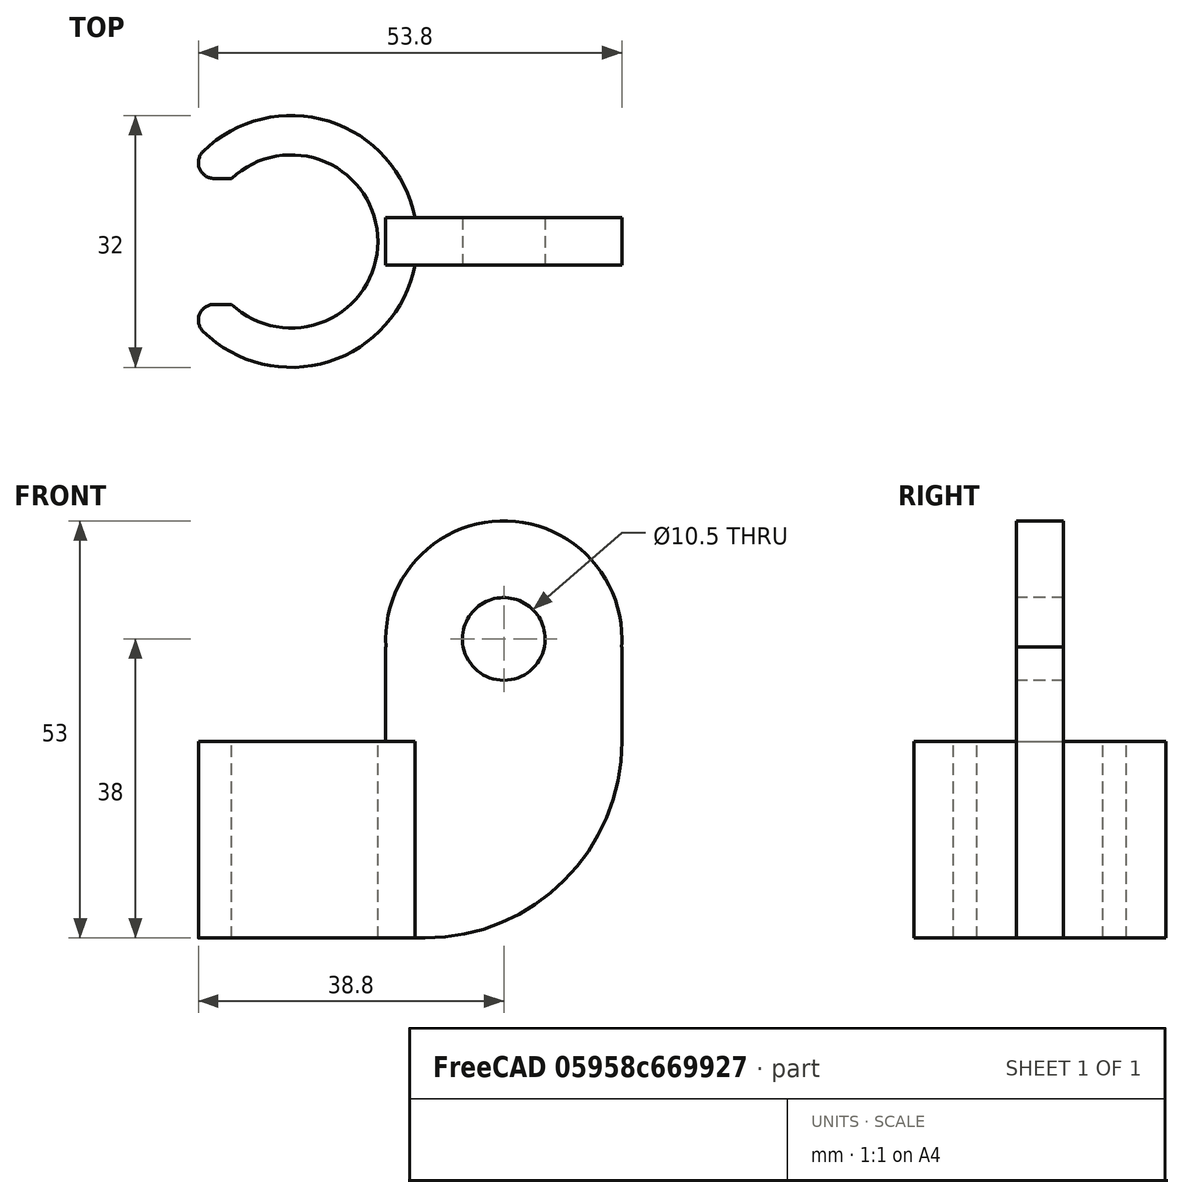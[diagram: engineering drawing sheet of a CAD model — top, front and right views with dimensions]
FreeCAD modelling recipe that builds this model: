
FCSTD DOCUMENT  (FreeCAD 0.18R4 (GitTag))
Label: Soporte_Ducha
License: All rights reserved
LicenseURL: http://en.wikipedia.org/wiki/All_rights_reserved
objects: Part::Cylinder×4, Part::Cut×3, Part::Box×2, Part::MultiFuse×2, Part::Fillet×2
note: 13 computed .brp shape members not serialized (recipe doc carries the construction recipe); baked Part::Feature solids carry a one-line shape summary decoded from their .brp

FEATURE [Part::Cylinder] Cylinder  label="Cilindro"
  Angle = 360
  AttacherType = Attacher::AttachEngine3D
  Height = 25
  Radius = 11
FEATURE [Part::Cylinder] Cylinder001  label="Cilindro001"
  Angle = 360
  AttacherType = Attacher::AttachEngine3D
  Height = 25
  Radius = 16
FEATURE [Part::Cut] Cut
  Base = -> Cylinder001
  Tool = -> Cylinder
FEATURE [Part::Box] Box  label="Cubo"
  AttacherType = Attacher::AttachEngine3D
  Height = 37
  Length = 30
  Placement = pos=(12,-3,0) rot=(0,0,1;0rad)
  Width = 6
FEATURE [Part::Cylinder] Cylinder002  label="Cilindro002"
  Angle = 360
  AttacherType = Attacher::AttachEngine3D
  Height = 6
  Placement = pos=(27,3,38) rot=(1,0,0;1.5708rad)
  Radius = 15
FEATURE [Part::Cylinder] Cylinder003  label="Cilindro003"
  Angle = 360
  AttacherType = Attacher::AttachEngine3D
  Height = 6
  Placement = pos=(27,3,38) rot=(1,0,0;1.5708rad)
  Radius = 5.25
FEATURE [Part::MultiFuse] Fusion
  Shapes = -> [Box,Cylinder002]
FEATURE [Part::Cut] Cut001
  Base = -> Fusion
  Tool = -> Cylinder003
FEATURE [Part::Box] Box001  label="Cubo001"
  AttacherType = Attacher::AttachEngine3D
  Height = 37
  Length = 30
  Placement = pos=(-24,-8,0) rot=(0,0,1;0rad)
  Width = 16
FEATURE [Part::Cut] Cut002
  Base = -> Cut
  Tool = -> Box001
FEATURE [Part::Fillet] Fillet
  Base = -> Cut002
  Edges = 2 edges r=2: [Edge3,Edge6]
FEATURE [Part::Fillet] Fillet001
  Base = -> Cut001
  Edges = 1 edges r=25: [Edge16]
FEATURE [Part::MultiFuse] Fusion001
  Shapes = -> [Fillet,Fillet001]
